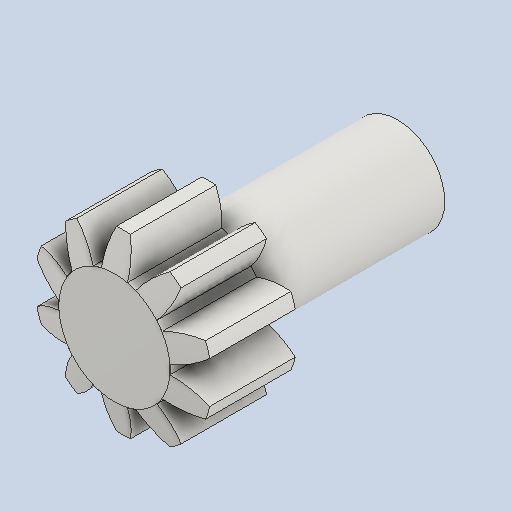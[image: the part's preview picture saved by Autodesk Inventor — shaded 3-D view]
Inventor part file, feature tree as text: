
AUTODESK INVENTOR PART (.ipt)
format: ipt  version: 2022 (Build 260153000, 153)  size: 265,216 bytes
history: native  units: in
note: dims shown in document units (in); Inventor stores cm internally (conversion verified against a paired STEP export)
features: other x12, sketch x6, plane x3
ambient origin geometry x8: Origin, YZ Plane, XZ Plane, XY Plane, X Axis, Y Axis, Z Axis, Center Point
bodies: Solid1 (feature_tree)
feature tree (21):
  other  "Spur Gear12_MIR.ipt"
  other  "Solid1::Spur Gear12_MIR.ipt"
  other  "TaggingFeature1"
  sketch  "Sketch1"  dims[d0=0.3937in]
  sketch  "Sketch2"  dims[d9=0.0in d14=0.0in d15=0.9352in d16=0.0in d17=0.0in d18=0.0in d19=0.9352in]
  sketch  "Sketch3"
  sketch  "Sketch4"
  sketch  "Sketch5"
  sketch  "Sketch6"
  plane  "XZ Plane_1"
  plane  "Work Plane2"
  plane  "Work Plane3"
  other  "Srf1"
  other  "Srf1::Derived"
  other  "Start plane iMate"
  other  "Distance iMate"
  other  "Position iMate"
  other  "Mesh iMate"
  other  "Axis iMate"
  other  "Mesh iMate2"
  other  "Align iMate"
